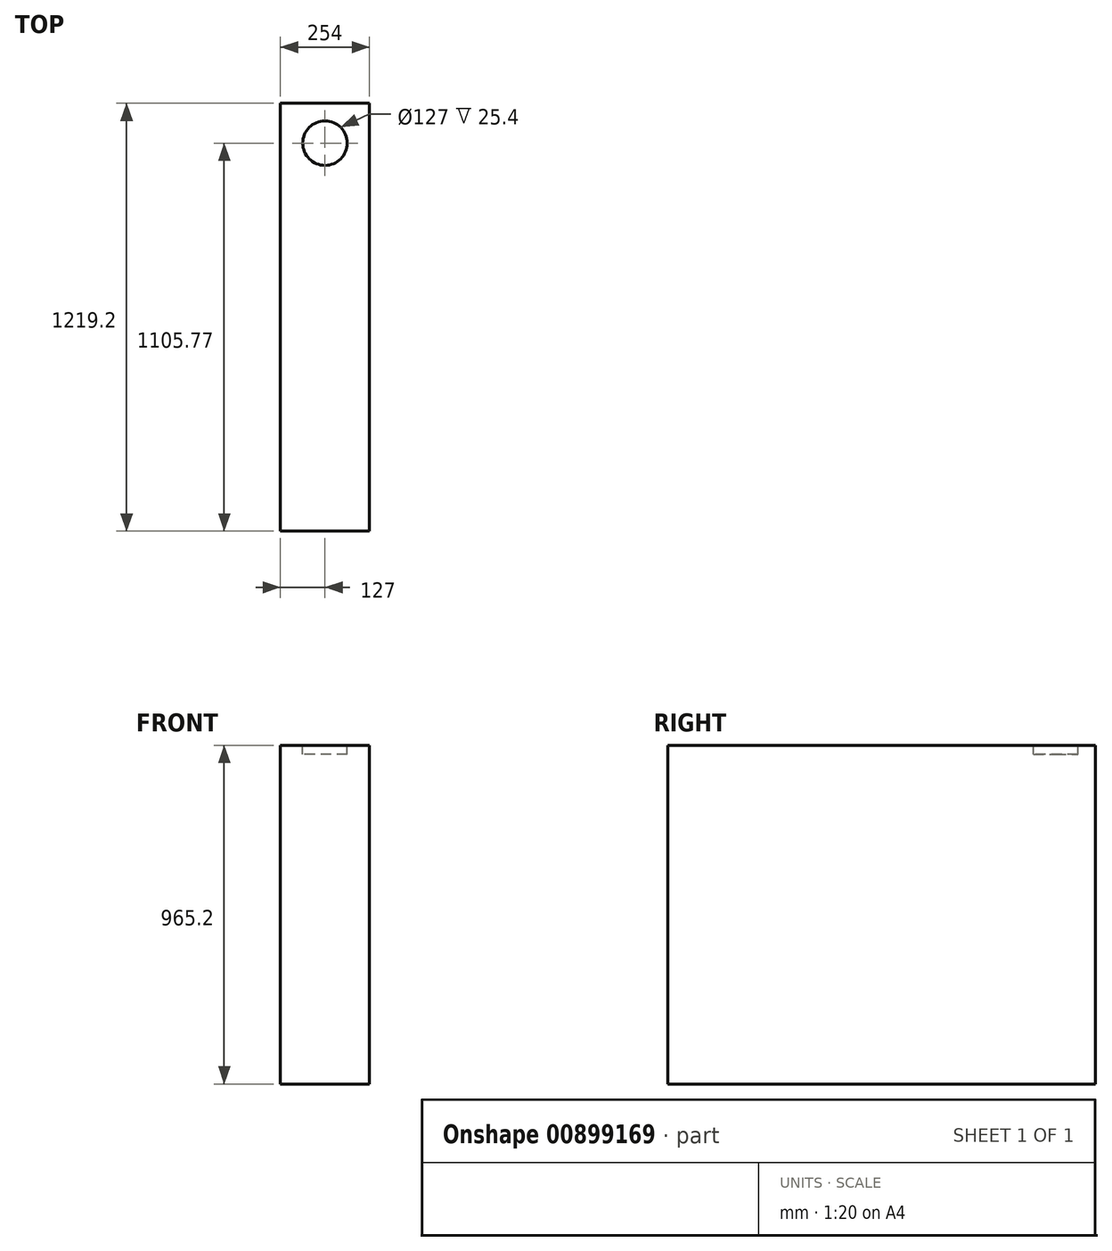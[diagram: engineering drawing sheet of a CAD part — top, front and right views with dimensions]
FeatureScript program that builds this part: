
annotation { "Feature Type Name" : "Feature", "Feature Type Description" : "" }
export const myFeature = defineFeature(function(context is Context, id is Id, definition is map)
    precondition{}
    {
        {
            var Q0;
            Q0=qCreatedBy(makeId("Top.planeOp"),FACE);
            var sketch = newSketch(context, id + "F0", { "sketchPlane" : qUnion([Q0])});
            skLineSegment(sketch, "E0.bottom", {"start": v(127, -609.6) * mm, "end": v(-127, -609.6) * mm});
            skLineSegment(sketch, "E0.top", {"start": v(127, 609.6) * mm, "end": v(-127, 609.6) * mm});
            skLineSegment(sketch, "E0.left", {"start": v(127, -609.6) * mm, "end": v(127, 609.6) * mm});
            skLineSegment(sketch, "E0.right", {"start": v(-127, -609.6) * mm, "end": v(-127, 609.6) * mm});
            skPoint(sketch, "E0.middle", {"position": v(0, 0) * mm});
            skSolve(sketch);
        }
        {
            var Q0;
            Q0=makeQuery(id+"F0.imprint","IMPRINT",FACE,{"disambiguationData":[TD([[makeQuery(id+"F0.imprint","IMPRINT",EDGE,{"derivedFrom":sQuery(id+"F0.wireOp",EDGE,"E0.bottom")}),-1.0]])]});
            extrude(context, id + "F1", {"entities" : qUnion([Q0]), "depth" : 965.2 * mm, "offsetDistance" : 25.4 * mm});
        }
        {
            var Q0;
            Q0=makeQuery(id+"F1.opExtrude","CAP_FACE",FACE,{"disambiguationData":[OSD([sQuery(id+"F0.wireOp",EDGE,"E0.bottom"),sQuery(id+"F0.wireOp",EDGE,"E0.top"),sQuery(id+"F0.wireOp",EDGE,"E0.left"),sQuery(id+"F0.wireOp",EDGE,"E0.right")])],"isStart":false});
            var sketch = newSketch(context, id + "F2", { "sketchPlane" : qUnion([Q0])});
            skCircle(sketch, "E1", {"center": v(0, 496.17) * mm, "radius": 63.5 * mm});
            skPoint(sketch, "E1.centerSnap0", {"position": v(0, 609.6) * mm});
            skSolve(sketch);
        }
        {
            var Q0;
            Q0=makeQuery(id+"F2.imprint","IMPRINT",FACE,{"disambiguationData":[TD([[makeQuery(id+"F2.imprint","IMPRINT",EDGE,{"derivedFrom":sQuery(id+"F2.wireOp",EDGE,"E1")}),1.0]])]});
            extrude(context, id + "F3", {"entities" : qUnion([Q0]), "operationType" : NewBodyOperationType.REMOVE, "oppositeDirection" : true, "depth" : 25.4 * mm, "offsetDistance" : 25.4 * mm});
        }
    });
